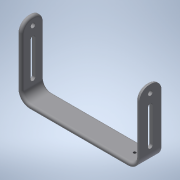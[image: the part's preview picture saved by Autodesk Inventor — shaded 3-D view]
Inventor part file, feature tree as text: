
AUTODESK INVENTOR PART (.ipt)
format: ipt  version: 2022 (Build 260153000, 153)  size: 257,024 bytes
history: native  units: mm
features: other x7, sketch x5, hole x2, fillet x1
ambient origin geometry x8: Origin, YZ Plane, XZ Plane, XY Plane, X Axis, Y Axis, Z Axis, Center Point
bodies: Volumenkörper1 (feature_tree)
feature tree (15):
  other  "Fläche1"
  sketch  "Skizze3"  dims[d2=3.0mm d17=44.0mm d18=44.0mm]
  other  "Falten3"
  other  "Falten4"
  other  "Eckenrundung1"
  hole  "Bohrung1"  [1 undecoded]
  hole  "Bohrung2"  [1 undecoded]
  fillet  "Rundung1"  Radius=44.0mm
  sketch  "Skizze1"  dims[d0=220.0mm d1=19.8mm]
  other  "Grobblech1"
  sketch  "Skizze4"  dims[d19=3.0mm]
  sketch  "Skizze5"  dims[d20=1.5mm]
  sketch  "Skizze6"  dims[d21=6.0mm d22=3.0mm d23=90.0deg d24=7.0mm d25=3.0mm d26=1.5mm d27=6.0mm d28=3.0mm d29=90.0deg d30=7.0mm d31=9.0mm d32=9.9mm d33=7.0mm d34=4.0mm d35=6.0mm d36=4.0mm d37=2.0mm d38=90.0deg d39=3.0mm d40=20.594885mm d41=9.9mm d42=13.0mm d43=4.2mm d44=35.0mm d45=3.0mm d46=0.0mm d47=40.0mm d48=2.459mm d49=6.0mm d50=4.0mm d51=2.0mm d52=90.0deg d53=3.0mm d54=20.594885mm d55=3.0mm d56=2.0mm]
  other  "Ausklinkung1"
  other  "Definition1"
note: 2 required parameter values undecoded (feature->parameter linkage not recoverable at this tier; creation-order binding heuristic only, values carry confidence <= 0.55)
